# Revit family: heroal S 77 Sliding Door - 2-Parts - D
name_source: partatom
category: Türen
revit_build: Autodesk Revit 2017 (Build: 20160225_1515(x64)
units: mm (PartAtom-declared; Revit-internal decimal feet)

## family parameters
Basisbauteil = Wand
Beim Laden mit Abzugskörper schneiden = Nein
Gemeinsam genutzt = Nein
Immer vertikal = Ja
OmniClass-Nummer = 23.30.10.00
OmniClass-Titel = Doors
Raumberechnungspunkt = Ja

## types (2) — shared parameters
Air Permeability DIN EN 12207 = 4
Analytische Konstruktion = <None>
Baugruppenkennzeichen = B2030110
Beschreibung = heroal S 77 Sliding Systems
Burglary Resistance DIN V ENV 1627 = up to RC 2
Edition number = 1
Glass = heroal Glass
Heat Insulation [Uf in W/m2K] DIN EN ISO 10077 = > 2,9 W/m²K
Heat Insulation [Uf in W/m2K]/Standard Profile View DIN EN ISO 10077 = > 2,9 W/m²K
Heat Insulation [Uw in W/m2K] DIN EN ISO 10077-1 = > 1,1 W/m²K
Hersteller = heroal
Höhe = 2200 mm
Max. Casement Leaf Height = 3000mm
Max. Casement Weight = 150 - 400kg
Max. Thickness Of Glass/Infill Panel = 52mm
Modell = heroal S 77
Profile Installation Depth - Casement Profiles = 77mm
Profile Installation Depth - Cross Bar Profiles = 72mm
Profile Installation Depth - Frame Profiles = 178/279mm
Profile View Width - Casement Profiles = 94 - 104mm
Profile View Width - Cross Bar Profiles = 74 - 104mm
Profile View Width - Frame Profiles = 40 - 63mm
Reveal Right = 20 mm  [stored 0.0656168 ft]
Reveal Top = 20 mm  [stored 0.0656168 ft]
Rohbauhöhe = 2200 mm
Soundproofing Class DIN EN ISO 717-1 = 1-3
Tightness Against Driving Rain DIN EN 12208 = 9A
URL = http://www.heroal.com
Wandabschluss = Nach Basisbauteil
Wind Load Resistance DIN EN 12210 = C3/B3

## per-type parameters (varying)
| type | Breite | Leaf Width | Reveal Left | Rohbaubreite |
| 2400x2200 No Reveal Left | 2400 mm | 1200 mm | 0 mm  [stored 0 ft] | 2400 mm |
| 2600x2200 | 2600 mm | 1300 mm  [stored 4.26509 ft] | 20 mm  [stored 0.0656168 ft] | 2600 mm |

note: [stored X ft] marks values corroborated as IEEE doubles in the binary element streams (Revit-internal decimal feet)

## geometry (parser evidence)
native form markers: Blend x1, Sweep x19
no freeform markers — native parametric forms only
